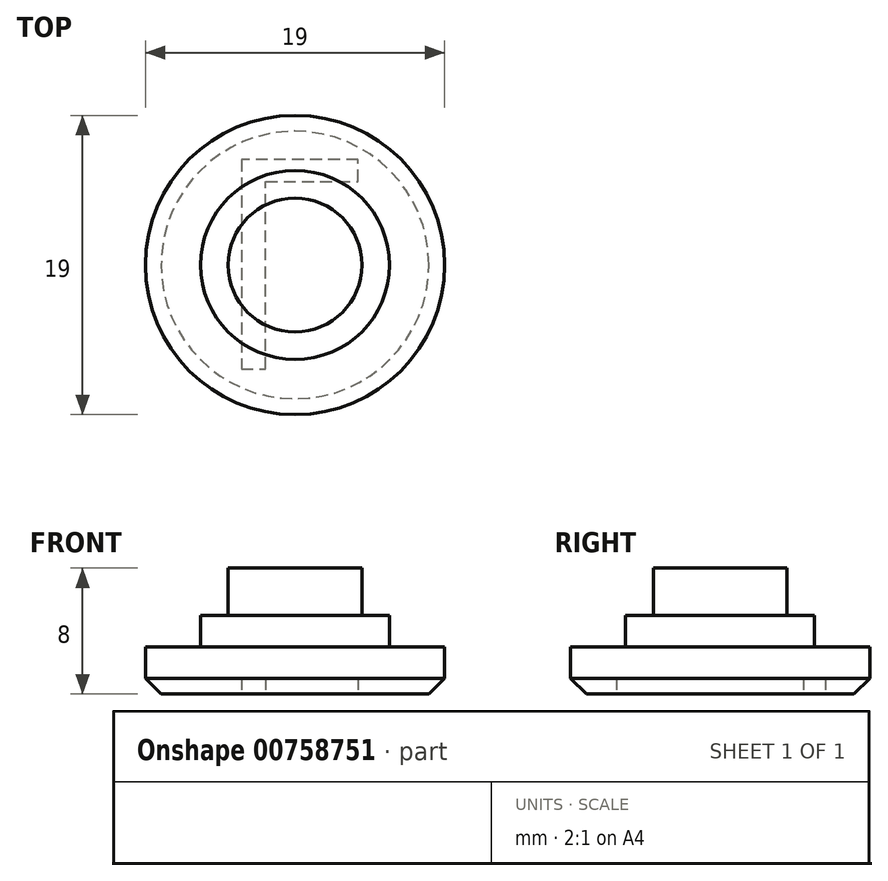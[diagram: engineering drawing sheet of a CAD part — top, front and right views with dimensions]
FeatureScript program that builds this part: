
annotation { "Feature Type Name" : "Feature", "Feature Type Description" : "" }
export const myFeature = defineFeature(function(context is Context, id is Id, definition is map)
    precondition{}
    {
        {
            assignVariable(context, id + "F0", {"name" : "clearance", "anyValue" : 2});
        }
        {
            assignVariable(context, id + "F1", {"name" : "capthick", "anyValue" : 3});
        }
        {
            var Q0;
            Q0=qCreatedBy(makeId("Top.planeOp"),FACE);
            var sketch = newSketch(context, id + "F2", { "sketchPlane" : qUnion([Q0])});
            skCircle(sketch, "E0", {"center": v(0, 0) * mm, "radius": 4.25 * mm});
            skCircle(sketch, "E1", {"center": v(0, 0) * mm, "radius": 6 * mm});
            skCircle(sketch, "E2", {"center": v(0, 0) * mm, "radius": 9.5 * mm});
            skSolve(sketch);
        }
        {
            var Q0;
            Q0=makeQuery(id+"F2.imprint","IMPRINT",FACE,{"disambiguationData":[TD([[makeQuery(id+"F2.imprint","IMPRINT",EDGE,{"derivedFrom":sQuery(id+"F2.wireOp",EDGE,"E1")}),-1.0]])]});
            extrude(context, id + "F3", {"entities" : qUnion([Q0]), "depth" : (getVariable(context, 'capthick')) * mm, "offsetDistance" : 25 * mm});
        }
        {
            var Q0;
            Q0=makeQuery(id+"F2.imprint","IMPRINT",FACE,{"disambiguationData":[TD([[makeQuery(id+"F2.imprint","IMPRINT",EDGE,{"derivedFrom":sQuery(id+"F2.wireOp",EDGE,"E0")}),-1.0]])]});
            extrude(context, id + "F4", {"entities" : qUnion([Q0]), "operationType" : NewBodyOperationType.ADD, "depth" : (getVariable(context, 'clearance') + getVariable(context, 'capthick')) * mm, "offsetDistance" : 25 * mm});
        }
        {
            var Q0;
            Q0=makeQuery(id+"F2.imprint","IMPRINT",FACE,{"disambiguationData":[TD([[makeQuery(id+"F2.imprint","IMPRINT",EDGE,{"derivedFrom":sQuery(id+"F2.wireOp",EDGE,"E0")}),1.0]])]});
            extrude(context, id + "F5", {"entities" : qUnion([Q0]), "operationType" : NewBodyOperationType.ADD, "depth" : (getVariable(context, 'clearance') + getVariable(context, 'capthick') + 3) * mm, "offsetDistance" : 25 * mm});
        }
        {
            var Q0;
            Q0=makeQuery(id+"F3.opExtrude","CAP_EDGE",EDGE,{"disambiguationData":[OSD([sQuery(id+"F2.wireOp",EDGE,"E2")])],"isStart":true});
            chamfer(context, id + "F6", {"entities" : qUnion([Q0]), "width" : 1 * mm, "tangentPropagation" : true});
        }
        {
            var Q0;
            {var subQ0=sQuery(id+"F2.wireOp",EDGE,"E0");var subQ1=sQuery(id+"F2.wireOp",EDGE,"E1");Q0=makeQuery(id+"F5.boolean.opBoolean","MERGE",FACE,{"derivedFrom":[makeQuery(id+"F4.boolean.opBoolean","MERGE",FACE,{"derivedFrom":[makeQuery(id+"F3.opExtrude","CAP_FACE",FACE,{"disambiguationData":[OSD([subQ1,sQuery(id+"F2.wireOp",EDGE,"E2")])],"isStart":true}),makeQuery(id+"F4.opExtrude","CAP_FACE",FACE,{"disambiguationData":[OSD([subQ0,subQ1])],"isStart":true})]}),makeQuery(id+"F5.opExtrude","CAP_FACE",FACE,{"disambiguationData":[OSD([subQ0])],"isStart":true})]});}
            var sketch = newSketch(context, id + "F7", { "sketchPlane" : qUnion([Q0])});
            skText(sketch, "E3", { "text": "L", "fontName": "OpenSans-Regular.ttf"});
            const initialGuessF7  = {"E3": [-0.00523, -0.0067, 1, 0, 0.01341]};
            skSetInitialGuess(sketch, initialGuessF7);
            skSolve(sketch);
        }
        {
            var Q0;
            Q0=makeQuery(id+"F7.imprint","IMPRINT",FACE,{"disambiguationData":[TD([[makeQuery(id+"F7.imprint","IMPRINT",EDGE,{"derivedFrom":sQuery(id+"F7.wireOp",EDGE,"E3.sketch_text.stroke-0")}),-1.0]])]});
            extrude(context, id + "F8", {"entities" : qUnion([Q0]), "operationType" : NewBodyOperationType.REMOVE, "oppositeDirection" : true, "depth" : 1 * mm, "offsetDistance" : 25 * mm});
        }
        {
            var Q0;
            Q0=makeQuery(id+"F7.imprint","IMPRINT",FACE,{"disambiguationData":[TD([[makeQuery(id+"F7.imprint","IMPRINT",EDGE,{"derivedFrom":sQuery(id+"F7.wireOp",EDGE,"E3.sketch_text.stroke-0")}),-1.0]])]});
            extrude(context, id + "F9", {"entities" : qUnion([Q0]), "operationType" : NewBodyOperationType.REMOVE, "oppositeDirection" : true, "depth" : 1 * mm, "offsetDistance" : 25 * mm});
        }
    });
